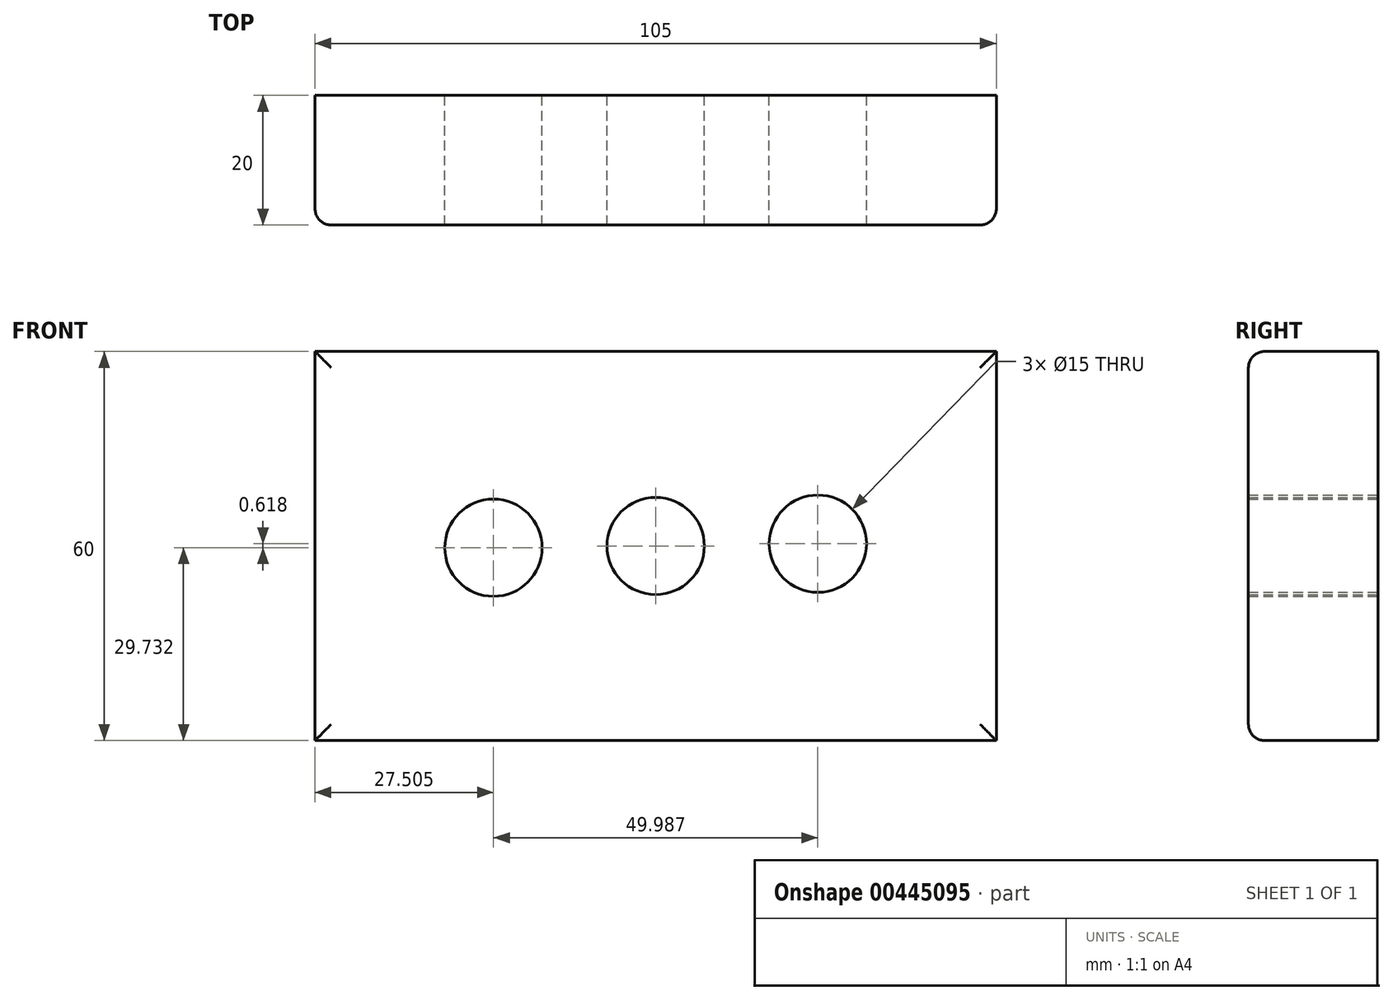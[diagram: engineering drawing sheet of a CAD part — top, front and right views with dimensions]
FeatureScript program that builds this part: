
annotation { "Feature Type Name" : "Feature", "Feature Type Description" : "" }
export const myFeature = defineFeature(function(context is Context, id is Id, definition is map)
    precondition{}
    {
        {
            var Q0;
            Q0=qCreatedBy(makeId("Front.planeOp"),FACE);
            var sketch = newSketch(context, id + "F0", { "sketchPlane" : qUnion([Q0])});
            skLineSegment(sketch, "E0.bottom", {"start": v(52.5, 30) * mm, "end": v(-52.5, 30) * mm});
            skLineSegment(sketch, "E0.top", {"start": v(52.5, -30) * mm, "end": v(-52.5, -30) * mm});
            skLineSegment(sketch, "E0.left", {"start": v(52.5, 30) * mm, "end": v(52.5, -30) * mm});
            skLineSegment(sketch, "E0.right", {"start": v(-52.5, 30) * mm, "end": v(-52.5, -30) * mm});
            skPoint(sketch, "E0.middle", {"position": v(0, 0) * mm});
            skCircle(sketch, "E1", {"center": v(0, 0) * mm, "radius": 7.5 * mm});
            skLineSegment(sketch, "E2", {"start": v(-7.5, 0) * mm, "end": v(-17.5, 0) * mm});
            skLineSegment(sketch, "E3", {"start": v(7.5, 0) * mm, "end": v(17.5, 0) * mm});
            skPoint(sketch, "E4.second.point", {"position": v(-32.5, 0) * mm});
            skCircle(sketch, "E5", {"center": v(-25, -0.27) * mm, "radius": 7.5 * mm});
            skPoint(sketch, "E5.third.point", {"position": v(-25.5, 7.22) * mm});
            skCircle(sketch, "E6", {"center": v(25, 0.35) * mm, "radius": 7.5 * mm});
            skPoint(sketch, "E6.second.point", {"position": v(32.48, 0) * mm});
            skPoint(sketch, "E6.third.point", {"position": v(31.34, 4.34) * mm});
            skSolve(sketch);
        }
        {
            var Q0;
            Q0 = qSketchRegion(id + "F0", true);
            extrude(context, id + "F1", {"entities" : qUnion([Q0]), "depth" : 20 * mm});
        }
        {
            var Q0;
            Q0=makeQuery(id+"F1.opExtrude","CAP_EDGE",EDGE,{"disambiguationData":[OSD([sQuery(id+"F0.wireOp",EDGE,"E0.right")])],"isStart":false});
            var Q1;
            Q1=makeQuery(id+"F1.opExtrude","CAP_EDGE",EDGE,{"disambiguationData":[OSD([sQuery(id+"F0.wireOp",EDGE,"E0.bottom")])],"isStart":false});
            var Q2;
            Q2=makeQuery(id+"F1.opExtrude","CAP_EDGE",EDGE,{"disambiguationData":[OSD([sQuery(id+"F0.wireOp",EDGE,"E0.left")])],"isStart":false});
            var Q3;
            Q3=makeQuery(id+"F1.opExtrude","CAP_EDGE",EDGE,{"disambiguationData":[OSD([sQuery(id+"F0.wireOp",EDGE,"E0.top")])],"isStart":false});
            fillet(context, id + "F2", {"entities" : qUnion([Q0, Q1, Q2, Q3]), "radius" : 2.5 * mm, "tangentPropagation" : true, "allowEdgeOverflow" : false});
        }
    });
